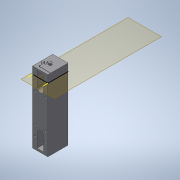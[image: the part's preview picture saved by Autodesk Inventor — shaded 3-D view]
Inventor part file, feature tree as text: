
AUTODESK INVENTOR PART (.ipt)
format: ipt  version: 2020 (Build 240168000, 168)  size: 235,008 bytes
history: native  units: mm
features: extrude x9, sketch x9, reference x8, other x6, projected_geometry x3, hole x1, mirror x1
ambient origin geometry x8: Origin, YZ Plane, XZ Plane, XY Plane, X Axis, Y Axis, Z Axis, Center Point
bodies: Body1 (feature_tree)
feature tree (37):
  other  "Bryła1"
  other  "Płaszczyzna konstrukcyjna1"
  extrude  "Wyciągnięcie proste1"  Depth=3.0mm TaperAngle=0.0deg
  extrude  "Wyciągnięcie proste2"  Depth=6.0mm
  extrude  "Wyciągnięcie proste3"  Depth=20.0mm TaperAngle=0.0deg
  sketch  "Szkic4"
  extrude  "Wyciągnięcie proste4"  Depth=0.25mm
  extrude  "Wyciągnięcie proste5"  Depth=0.25mm
  hole  "Otwór3"  [1 undecoded]
  extrude  "Wyciągnięcie proste6"  Depth=0.25mm
  extrude  "Wyciągnięcie proste7"  TaperAngle=0.0deg  [1 undecoded]
  mirror  "Odbij1"
  extrude  "Wyciągnięcie proste8"  Depth=14.6mm
  extrude  "Wyciągnięcie proste9"  TaperAngle=0.0deg  [1 undecoded]
  sketch  "Szkic1"
  reference  "Odniesienie1"
  reference  "Odniesienie2"
  sketch  "Szkic2"
  sketch  "Szkic3"
  reference  "Odniesienie3"
  reference  "Odniesienie4"
  reference  "Odniesienie5"
  reference  "Odniesienie6"
  reference  "Odniesienie7"
  sketch  "Szkic6"
  projected_geometry  "Pętla rzutowana1"
  sketch  "Szkic7"
  reference  "Odniesienie8"
  sketch  "Szkic8"
  projected_geometry  "Pętla rzutowana2"
  sketch  "Szkic9"
  projected_geometry  "Pętla rzutowana3"
  sketch  "Szkic11"
  other  "<userpath>\Desktop\3d\scanning-robot\Assembly1.iam"
  other  "Assembly1.iam"
  other  "wheel-adapter:1"
  other  "wheel-adapter-front_MIR:1"
note: 3 required parameter values undecoded (feature->parameter linkage not recoverable at this tier; creation-order binding heuristic only, values carry confidence <= 0.55)
